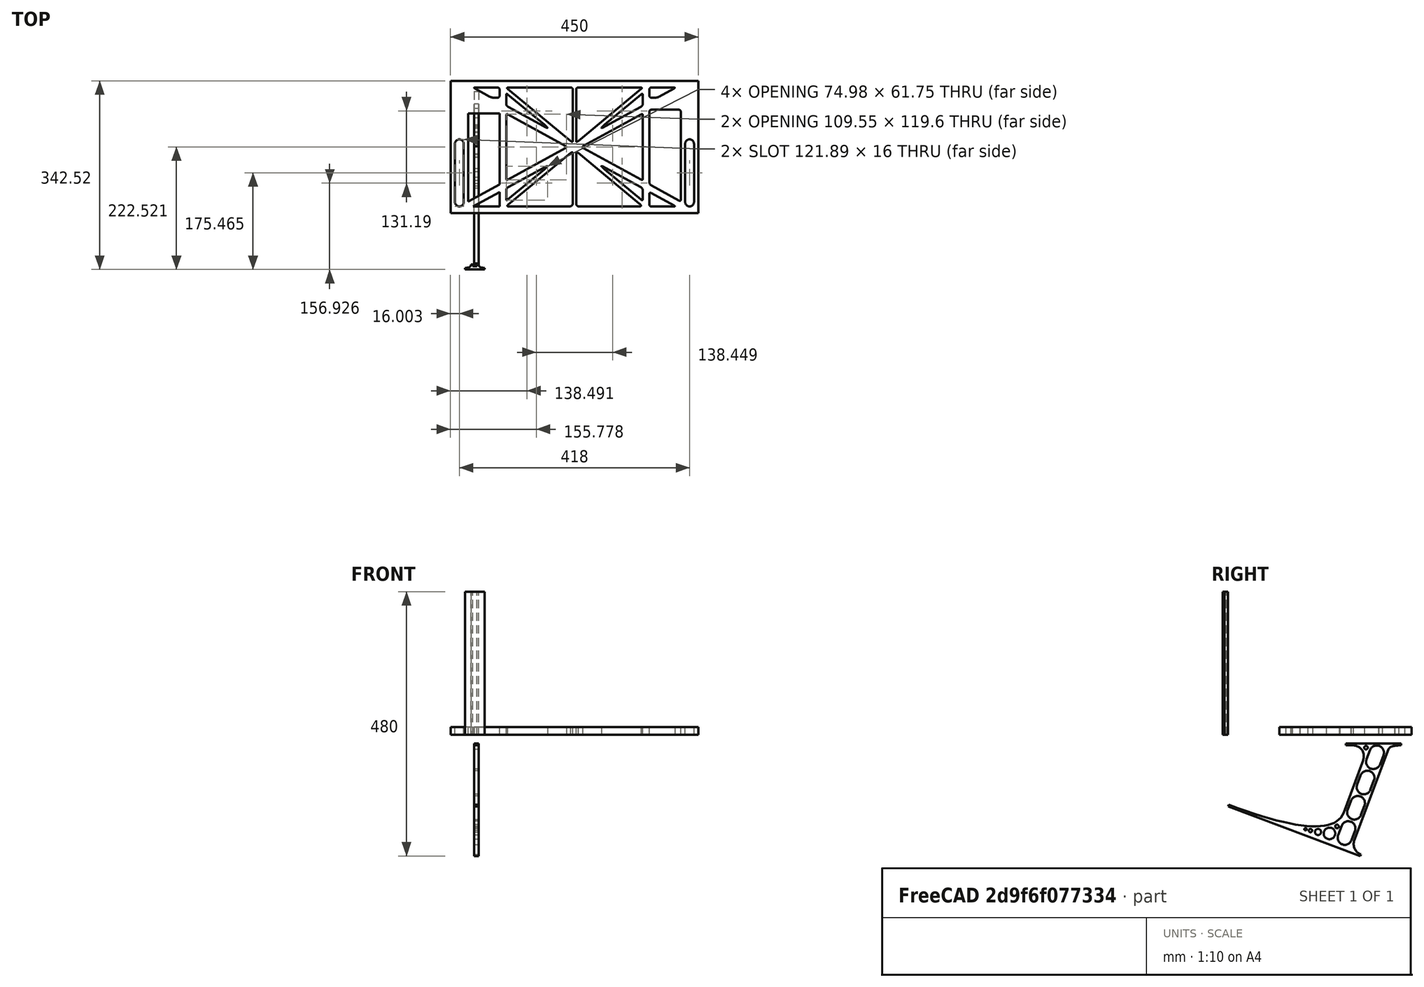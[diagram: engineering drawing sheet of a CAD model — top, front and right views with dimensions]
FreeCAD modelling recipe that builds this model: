
FCSTD DOCUMENT  (FreeCAD 0.19R0.19.2)
Label: laptopStand121FCStd
License: All rights reserved
LicenseURL: http://en.wikipedia.org/wiki/All_rights_reserved
objects: Sketcher::SketchObject×3, Part::Extrusion×3
note: 6 computed .brp shape members not serialized (recipe doc carries the construction recipe); baked Part::Feature solids carry a one-line shape summary decoded from their .brp

FEATURE [Sketcher::SketchObject] Sketch
  FullyConstrained = false
  sketch-geometry (339):
    g0: LineSegment StartX=-10.9272 StartY=-82.7794 StartZ=0 EndX=46.0728 EndY=-51.4823 EndZ=0
    g1: LineSegment StartX=-10.9272 StartY=77.3346 StartZ=0 EndX=-10.9272 EndY=-82.7794 EndZ=0
    g2: LineSegment StartX=-1.92719 StartY=-91.7794 StartZ=0 EndX=46.0728 EndY=-91.7794 EndZ=0
    g3: LineSegment StartX=46.0728 StartY=-65.424 StartZ=0 EndX=-1.92719 EndY=-91.7794 EndZ=0
    g4: LineSegment StartX=46.0728 StartY=-65.424 StartZ=0 EndX=46.0728 EndY=-91.7794 EndZ=0
    g5: LineSegment StartX=46.0728 StartY=77.3346 StartZ=0 EndX=46.0728 EndY=-51.4823 EndZ=0
    g6: LineSegment StartX=-42.9272 StartY=136.221 StartZ=0 EndX=-42.9272 EndY=-103.779 EndZ=0
    g7: LineSegment StartX=407.073 StartY=136.221 StartZ=0 EndX=407.073 EndY=-103.779 EndZ=0
    g8: ArcOfCircle CenterX=-26.9272 CenterY=22.1087 CenterZ=0 NormalX=0 NormalY=0 NormalZ=1 AngleXU=0 Radius=8 StartAngle=1e-16 EndAngle=3.14159
    g9: ArcOfCircle CenterX=-26.9272 CenterY=-83.7794 CenterZ=0 NormalX=0 NormalY=0 NormalZ=1 AngleXU=0 Radius=8 StartAngle=3.14159 EndAngle=6.28319
    g10: LineSegment StartX=-34.9272 StartY=22.1087 StartZ=0 EndX=-34.9272 EndY=-83.7794 EndZ=0
    g11: LineSegment StartX=-18.9272 StartY=22.1087 StartZ=0 EndX=-18.9272 EndY=-83.7794 EndZ=0
    g12: ArcOfCircle CenterX=391.073 CenterY=22.1087 CenterZ=0 NormalX=0 NormalY=0 NormalZ=1 AngleXU=0 Radius=8 StartAngle=-4.4e-15 EndAngle=3.14159
    g13: LineSegment StartX=399.073 StartY=22.1087 StartZ=0 EndX=399.073 EndY=-83.7794 EndZ=0
    g14: LineSegment StartX=383.073 StartY=22.1087 StartZ=0 EndX=383.073 EndY=-83.7794 EndZ=0
    g15: ArcOfCircle CenterX=391.073 CenterY=-83.7794 CenterZ=0 NormalX=0 NormalY=0 NormalZ=1 AngleXU=0 Radius=8 StartAngle=3.14159 EndAngle=6.28319
    g16: Circle CenterX=175.022 CenterY=27.0628 CenterZ=0 NormalX=0 NormalY=0 NormalZ=1 AngleXU=0 Radius=1
    g17: Circle CenterX=179.022 CenterY=24.8665 CenterZ=0 NormalX=0 NormalY=0 NormalZ=1 AngleXU=0 Radius=1
    g18: Circle CenterX=179.022 CenterY=27.0628 CenterZ=0 NormalX=0 NormalY=0 NormalZ=1 AngleXU=0 Radius=1
    g19: BSplineCurve PolesCount=3 KnotsCount=2 Degree=2 IsPeriodic=0
    g20: GeomPoint X=175.022 Y=27.0628 Z=0
    g21: GeomPoint X=179.022 Y=27.0628 Z=0
    g22: Circle CenterX=189.124 CenterY=27.0628 CenterZ=0 NormalX=0 NormalY=0 NormalZ=1 AngleXU=0 Radius=1
    g23: Circle CenterX=185.124 CenterY=24.8665 CenterZ=0 NormalX=0 NormalY=0 NormalZ=1 AngleXU=0 Radius=1
    g24: Circle CenterX=185.124 CenterY=27.0628 CenterZ=0 NormalX=0 NormalY=0 NormalZ=1 AngleXU=0 Radius=1
    g25: BSplineCurve PolesCount=3 KnotsCount=2 Degree=2 IsPeriodic=0
    g26: GeomPoint X=189.124 Y=27.0628 Z=0
    g27: GeomPoint X=185.124 Y=27.0628 Z=0
    g28: Circle CenterX=175.022 CenterY=5.37834 CenterZ=0 NormalX=0 NormalY=0 NormalZ=1 AngleXU=0 Radius=1
    g29: Circle CenterX=179.022 CenterY=7.57463 CenterZ=0 NormalX=0 NormalY=0 NormalZ=1 AngleXU=0 Radius=1
    g30: Circle CenterX=179.022 CenterY=5.34704 CenterZ=0 NormalX=0 NormalY=0 NormalZ=1 AngleXU=0 Radius=1
    g31: BSplineCurve PolesCount=3 KnotsCount=2 Degree=2 IsPeriodic=0
    g32: GeomPoint X=175.022 Y=5.37834 Z=0
    g33: GeomPoint X=179.022 Y=5.34704 Z=0
    g34: Circle CenterX=189.124 CenterY=5.37834 CenterZ=0 NormalX=0 NormalY=0 NormalZ=1 AngleXU=0 Radius=1
    g35: Circle CenterX=185.124 CenterY=7.57463 CenterZ=0 NormalX=0 NormalY=0 NormalZ=1 AngleXU=0 Radius=1
    g36: Circle CenterX=185.124 CenterY=5.34704 CenterZ=0 NormalX=0 NormalY=0 NormalZ=1 AngleXU=0 Radius=1
    g37: BSplineCurve PolesCount=3 KnotsCount=2 Degree=2 IsPeriodic=0
    g38: GeomPoint X=189.124 Y=5.37834 Z=0
    g39: GeomPoint X=185.124 Y=5.34704 Z=0
    g40: Circle CenterX=165.871 CenterY=18.1458 CenterZ=0 NormalX=0 NormalY=0 NormalZ=1 AngleXU=0 Radius=1
    g41: Circle CenterX=169.377 CenterY=16.2206 CenterZ=0 NormalX=0 NormalY=0 NormalZ=1 AngleXU=0 Radius=1
    g42: Circle CenterX=165.871 CenterY=14.2954 CenterZ=0 NormalX=0 NormalY=0 NormalZ=1 AngleXU=0 Radius=1
    g43: BSplineCurve PolesCount=3 KnotsCount=2 Degree=2 IsPeriodic=0
    g44: GeomPoint X=165.871 Y=18.1458 Z=0
    g45: GeomPoint X=165.871 Y=14.2954 Z=0
    g46: Circle CenterX=198.275 CenterY=18.1458 CenterZ=0 NormalX=0 NormalY=0 NormalZ=1 AngleXU=0 Radius=1
    g47: Circle CenterX=194.768 CenterY=16.2206 CenterZ=0 NormalX=0 NormalY=0 NormalZ=1 AngleXU=0 Radius=1
    g48: Circle CenterX=198.275 CenterY=14.2954 CenterZ=0 NormalX=0 NormalY=0 NormalZ=1 AngleXU=0 Radius=1
    g49: BSplineCurve PolesCount=3 KnotsCount=2 Degree=2 IsPeriodic=0
    g50: GeomPoint X=198.275 Y=18.1458 Z=0
    g51: GeomPoint X=198.275 Y=14.2954 Z=0
    g52: LineSegment StartX=407.073 StartY=-103.779 StartZ=0 EndX=-42.9272 EndY=-103.779 EndZ=0
    g53: LineSegment StartX=407.073 StartY=136.221 StartZ=0 EndX=-42.9272 EndY=136.221 EndZ=0
    g54: LineSegment StartX=46.0728 StartY=77.3346 StartZ=0 EndX=-10.9272 EndY=77.3346 EndZ=0
    g55: Circle CenterX=125.607 CenterY=54.1951 CenterZ=0 NormalX=0 NormalY=0 NormalZ=1 AngleXU=0 Radius=1
    g56: Circle CenterX=139.632 CenterY=46.4944 CenterZ=0 NormalX=0 NormalY=0 NormalZ=1 AngleXU=0 Radius=1
    g57: Circle CenterX=127.326 CenterY=56.7187 CenterZ=0 NormalX=0 NormalY=0 NormalZ=1 AngleXU=0 Radius=1
    g58: BSplineCurve PolesCount=3 KnotsCount=2 Degree=2 IsPeriodic=0
    g59: GeomPoint X=125.607 Y=54.1951 Z=0
    g60: GeomPoint X=127.326 Y=56.7187 Z=0
    g61: Circle CenterX=236.821 CenterY=56.7187 CenterZ=0 NormalX=0 NormalY=0 NormalZ=1 AngleXU=0 Radius=1
    g62: Circle CenterX=224.513 CenterY=46.4944 CenterZ=0 NormalX=0 NormalY=0 NormalZ=1 AngleXU=0 Radius=1
    g63: Circle CenterX=238.538 CenterY=54.1951 CenterZ=0 NormalX=0 NormalY=0 NormalZ=1 AngleXU=0 Radius=1
    g64: BSplineCurve PolesCount=3 KnotsCount=2 Degree=2 IsPeriodic=0
    g65: GeomPoint X=236.821 Y=56.7187 Z=0
    g66: GeomPoint X=238.538 Y=54.1951 Z=0
    g67: Circle CenterX=238.538 CenterY=-21.7539 CenterZ=0 NormalX=0 NormalY=0 NormalZ=1 AngleXU=0 Radius=1
    g68: Circle CenterX=224.513 CenterY=-14.0532 CenterZ=0 NormalX=0 NormalY=0 NormalZ=1 AngleXU=0 Radius=1
    g69: Circle CenterX=236.821 CenterY=-24.2775 CenterZ=0 NormalX=0 NormalY=0 NormalZ=1 AngleXU=0 Radius=1
    g70: BSplineCurve PolesCount=3 KnotsCount=2 Degree=2 IsPeriodic=0
    g71: GeomPoint X=238.538 Y=-21.7539 Z=0
    g72: GeomPoint X=236.821 Y=-24.2775 Z=0
    g73: Circle CenterX=125.607 CenterY=-21.7539 CenterZ=0 NormalX=0 NormalY=0 NormalZ=1 AngleXU=0 Radius=1
    g74: Circle CenterX=139.632 CenterY=-14.0532 CenterZ=0 NormalX=0 NormalY=0 NormalZ=1 AngleXU=0 Radius=1
    g75: Circle CenterX=127.325 CenterY=-24.2775 CenterZ=0 NormalX=0 NormalY=0 NormalZ=1 AngleXU=0 Radius=1
    g76: BSplineCurve PolesCount=3 KnotsCount=2 Degree=2 IsPeriodic=0
    g77: GeomPoint X=125.607 Y=-21.7539 Z=0
    g78: GeomPoint X=127.325 Y=-24.2775 Z=0
    g79: Circle CenterX=302.996 CenterY=111.695 CenterZ=0 NormalX=0 NormalY=0 NormalZ=1 AngleXU=0 Radius=1
    g80: Circle CenterX=306.073 CenterY=114.251 CenterZ=0 NormalX=0 NormalY=0 NormalZ=1 AngleXU=0 Radius=1
    g81: Circle CenterX=306.073 CenterY=110.251 CenterZ=0 NormalX=0 NormalY=0 NormalZ=1 AngleXU=0 Radius=1
    g82: BSplineCurve PolesCount=3 KnotsCount=2 Degree=2 IsPeriodic=0
    g83: GeomPoint X=302.996 Y=111.695 Z=0
    g84: GeomPoint X=306.073 Y=110.251 Z=0
    g85: Circle CenterX=306.073 CenterY=95.2763 CenterZ=0 NormalX=0 NormalY=0 NormalZ=1 AngleXU=0 Radius=1
    g86: Circle CenterX=306.073 CenterY=91.2763 CenterZ=0 NormalX=0 NormalY=0 NormalZ=1 AngleXU=0 Radius=1
    g87: Circle CenterX=302.567 CenterY=89.3511 CenterZ=0 NormalX=0 NormalY=0 NormalZ=1 AngleXU=0 Radius=1
    g88: BSplineCurve PolesCount=3 KnotsCount=2 Degree=2 IsPeriodic=0
    g89: GeomPoint X=306.073 Y=95.2763 Z=0
    g90: GeomPoint X=302.567 Y=89.3511 Z=0
    g91: LineSegment StartX=306.073 StartY=110.251 StartZ=0 EndX=306.073 EndY=95.2763 EndZ=0
    g92: LineSegment StartX=302.996 StartY=111.695 StartZ=0 EndX=236.821 EndY=56.7187 EndZ=0
    g93: LineSegment StartX=238.538 StartY=54.1951 StartZ=0 EndX=302.567 EndY=89.3511 EndZ=0
    g94: Circle CenterX=61.1496 CenterY=111.695 CenterZ=0 NormalX=0 NormalY=0 NormalZ=1 AngleXU=0 Radius=1
    g95: Circle CenterX=58.0728 CenterY=114.251 CenterZ=0 NormalX=0 NormalY=0 NormalZ=1 AngleXU=0 Radius=1
    g96: Circle CenterX=58.0728 CenterY=110.251 CenterZ=0 NormalX=0 NormalY=0 NormalZ=1 AngleXU=0 Radius=1
    g97: BSplineCurve PolesCount=3 KnotsCount=2 Degree=2 IsPeriodic=0
    g98: GeomPoint X=61.1496 Y=111.695 Z=0
    g99: GeomPoint X=58.0728 Y=110.251 Z=0
    g100: Circle CenterX=61.5791 CenterY=89.3511 CenterZ=0 NormalX=0 NormalY=0 NormalZ=1 AngleXU=0 Radius=1
    g101: Circle CenterX=58.0728 CenterY=91.2763 CenterZ=0 NormalX=0 NormalY=0 NormalZ=1 AngleXU=0 Radius=1
    g102: Circle CenterX=58.0728 CenterY=95.2763 CenterZ=0 NormalX=0 NormalY=0 NormalZ=1 AngleXU=0 Radius=1
    g103: BSplineCurve PolesCount=3 KnotsCount=2 Degree=2 IsPeriodic=0
    g104: GeomPoint X=61.5791 Y=89.3511 Z=0
    g105: GeomPoint X=58.0728 Y=95.2763 Z=0
    g106: LineSegment StartX=58.0728 StartY=110.251 StartZ=0 EndX=58.0728 EndY=95.2763 EndZ=0
    g107: LineSegment StartX=61.1496 StartY=111.695 StartZ=0 EndX=127.326 EndY=56.7187 EndZ=0
    g108: LineSegment StartX=125.607 StartY=54.1951 StartZ=0 EndX=61.5791 EndY=89.3511 EndZ=0
    g109: Circle CenterX=61.5791 CenterY=-56.9099 CenterZ=0 NormalX=0 NormalY=0 NormalZ=1 AngleXU=0 Radius=1
    g110: Circle CenterX=58.0728 CenterY=-58.8351 CenterZ=0 NormalX=0 NormalY=0 NormalZ=1 AngleXU=0 Radius=1
    g111: Circle CenterX=58.0728 CenterY=-62.8351 CenterZ=0 NormalX=0 NormalY=0 NormalZ=1 AngleXU=0 Radius=1
    g112: BSplineCurve PolesCount=3 KnotsCount=2 Degree=2 IsPeriodic=0
    g113: GeomPoint X=61.5791 Y=-56.9099 Z=0
    g114: GeomPoint X=58.0728 Y=-62.8351 Z=0
    g115: Circle CenterX=58.0728 CenterY=-77.8102 CenterZ=0 NormalX=0 NormalY=0 NormalZ=1 AngleXU=0 Radius=1
    g116: Circle CenterX=58.0728 CenterY=-81.8102 CenterZ=0 NormalX=0 NormalY=0 NormalZ=1 AngleXU=0 Radius=1
    g117: Circle CenterX=61.1496 CenterY=-79.2541 CenterZ=0 NormalX=0 NormalY=0 NormalZ=1 AngleXU=0 Radius=1
    g118: BSplineCurve PolesCount=3 KnotsCount=2 Degree=2 IsPeriodic=0
    g119: GeomPoint X=58.0728 Y=-77.8102 Z=0
    g120: GeomPoint X=61.1496 Y=-79.2541 Z=0
    g121: LineSegment StartX=58.0728 StartY=-62.8351 StartZ=0 EndX=58.0728 EndY=-77.8102 EndZ=0
    g122: LineSegment StartX=61.1496 StartY=-79.2541 StartZ=0 EndX=127.325 EndY=-24.2775 EndZ=0
    g123: LineSegment StartX=125.607 StartY=-21.7539 StartZ=0 EndX=61.5791 EndY=-56.9099 EndZ=0
    g124: Circle CenterX=302.567 CenterY=-56.9099 CenterZ=0 NormalX=0 NormalY=0 NormalZ=1 AngleXU=0 Radius=1
    g125: Circle CenterX=306.073 CenterY=-58.8351 CenterZ=0 NormalX=0 NormalY=0 NormalZ=1 AngleXU=0 Radius=1
    g126: Circle CenterX=306.073 CenterY=-62.8351 CenterZ=0 NormalX=0 NormalY=0 NormalZ=1 AngleXU=0 Radius=1
    g127: BSplineCurve PolesCount=3 KnotsCount=2 Degree=2 IsPeriodic=0
    g128: GeomPoint X=302.567 Y=-56.9099 Z=0
    g129: GeomPoint X=306.073 Y=-62.8351 Z=0
    g130: Circle CenterX=302.996 CenterY=-79.2541 CenterZ=0 NormalX=0 NormalY=0 NormalZ=1 AngleXU=0 Radius=1
    g131: Circle CenterX=306.073 CenterY=-81.8102 CenterZ=0 NormalX=0 NormalY=0 NormalZ=1 AngleXU=0 Radius=1
    g132: Circle CenterX=306.073 CenterY=-77.8102 CenterZ=0 NormalX=0 NormalY=0 NormalZ=1 AngleXU=0 Radius=1
    g133: BSplineCurve PolesCount=3 KnotsCount=2 Degree=2 IsPeriodic=0
    g134: GeomPoint X=302.996 Y=-79.2541 Z=0
    g135: GeomPoint X=306.073 Y=-77.8102 Z=0
    g136: LineSegment StartX=306.073 StartY=-62.8351 StartZ=0 EndX=306.073 EndY=-77.8102 EndZ=0
    g137: LineSegment StartX=302.996 StartY=-79.2541 StartZ=0 EndX=236.821 EndY=-24.2775 EndZ=0
    g138: LineSegment StartX=238.538 StartY=-21.7539 StartZ=0 EndX=302.567 EndY=-56.9099 EndZ=0
    g139: Circle CenterX=61.6457 CenterY=-88.8112 CenterZ=0 NormalX=0 NormalY=0 NormalZ=1 AngleXU=0 Radius=1
    g140: Circle CenterX=58.0728 CenterY=-91.7794 CenterZ=0 NormalX=0 NormalY=0 NormalZ=1 AngleXU=0 Radius=1
    g141: Circle CenterX=63.9135 CenterY=-91.7794 CenterZ=0 NormalX=0 NormalY=0 NormalZ=1 AngleXU=0 Radius=1
    g142: BSplineCurve PolesCount=3 KnotsCount=2 Degree=2 IsPeriodic=0
    g143: GeomPoint X=61.6457 Y=-88.8112 Z=0
    g144: GeomPoint X=63.9135 Y=-91.7794 Z=0
    g145: Circle CenterX=179.022 CenterY=-85.8163 CenterZ=0 NormalX=0 NormalY=0 NormalZ=1 AngleXU=0 Radius=1
    g146: Circle CenterX=179.022 CenterY=-91.7794 CenterZ=0 NormalX=0 NormalY=0 NormalZ=1 AngleXU=0 Radius=1
    g147: Circle CenterX=171.895 CenterY=-91.7794 CenterZ=0 NormalX=0 NormalY=0 NormalZ=1 AngleXU=0 Radius=1
    g148: BSplineCurve PolesCount=3 KnotsCount=2 Degree=2 IsPeriodic=0
    g149: GeomPoint X=179.022 Y=-85.8163 Z=0
    g150: GeomPoint X=171.895 Y=-91.7794 Z=0
    g151: Circle CenterX=185.124 CenterY=-86.2028 CenterZ=0 NormalX=0 NormalY=0 NormalZ=1 AngleXU=0 Radius=1
    g152: Circle CenterX=185.124 CenterY=-91.7794 CenterZ=0 NormalX=0 NormalY=0 NormalZ=1 AngleXU=0 Radius=1
    g153: Circle CenterX=191.747 CenterY=-91.7794 CenterZ=0 NormalX=0 NormalY=0 NormalZ=1 AngleXU=0 Radius=1
    g154: BSplineCurve PolesCount=3 KnotsCount=2 Degree=2 IsPeriodic=0
    g155: GeomPoint X=185.124 Y=-86.2028 Z=0
    g156: GeomPoint X=191.747 Y=-91.7794 Z=0
    g157: Circle CenterX=299.888 CenterY=-86.6413 CenterZ=0 NormalX=0 NormalY=0 NormalZ=1 AngleXU=0 Radius=1
    g158: Circle CenterX=306.073 CenterY=-91.7794 CenterZ=0 NormalX=0 NormalY=0 NormalZ=1 AngleXU=0 Radius=1
    g159: Circle CenterX=298.776 CenterY=-91.7794 CenterZ=0 NormalX=0 NormalY=0 NormalZ=1 AngleXU=0 Radius=1
    g160: BSplineCurve PolesCount=3 KnotsCount=2 Degree=2 IsPeriodic=0
    g161: GeomPoint X=299.888 Y=-86.6413 Z=0
    g162: GeomPoint X=298.776 Y=-91.7794 Z=0
    g163: LineSegment StartX=189.124 StartY=5.37834 StartZ=0 EndX=299.888 EndY=-86.6413 EndZ=0
    g164: LineSegment StartX=298.776 StartY=-91.7794 StartZ=0 EndX=191.747 EndY=-91.7794 EndZ=0
    g165: LineSegment StartX=185.124 StartY=-86.2028 StartZ=0 EndX=185.124 EndY=5.34704 EndZ=0
    g166: LineSegment StartX=179.022 StartY=5.34704 StartZ=0 EndX=179.022 EndY=-85.8163 EndZ=0
    g167: LineSegment StartX=171.895 StartY=-91.7794 StartZ=0 EndX=63.9135 EndY=-91.7794 EndZ=0
    g168: LineSegment StartX=61.6457 StartY=-88.8112 StartZ=0 EndX=175.022 EndY=5.37834 EndZ=0
    g169: Circle CenterX=302.073 CenterY=124.221 CenterZ=0 NormalX=0 NormalY=0 NormalZ=1 AngleXU=0 Radius=1
    g170: Circle CenterX=306.073 CenterY=124.221 CenterZ=0 NormalX=0 NormalY=0 NormalZ=1 AngleXU=0 Radius=1
    g171: Circle CenterX=302.996 CenterY=121.665 CenterZ=0 NormalX=0 NormalY=0 NormalZ=1 AngleXU=0 Radius=1
    g172: BSplineCurve PolesCount=3 KnotsCount=2 Degree=2 IsPeriodic=0
    g173: GeomPoint X=302.073 Y=124.221 Z=0
    g174: GeomPoint X=302.996 Y=121.665 Z=0
    g175: Circle CenterX=189.124 CenterY=124.221 CenterZ=0 NormalX=0 NormalY=0 NormalZ=1 AngleXU=0 Radius=1
    g176: Circle CenterX=185.124 CenterY=124.221 CenterZ=0 NormalX=0 NormalY=0 NormalZ=1 AngleXU=0 Radius=1
    g177: Circle CenterX=185.124 CenterY=120.221 CenterZ=0 NormalX=0 NormalY=0 NormalZ=1 AngleXU=0 Radius=1
    g178: BSplineCurve PolesCount=3 KnotsCount=2 Degree=2 IsPeriodic=0
    g179: GeomPoint X=189.124 Y=124.221 Z=0
    g180: GeomPoint X=185.124 Y=120.221 Z=0
    g181: Circle CenterX=175.022 CenterY=124.221 CenterZ=0 NormalX=0 NormalY=0 NormalZ=1 AngleXU=0 Radius=1
    g182: Circle CenterX=179.022 CenterY=124.221 CenterZ=0 NormalX=0 NormalY=0 NormalZ=1 AngleXU=0 Radius=1
    g183: Circle CenterX=179.022 CenterY=120.221 CenterZ=0 NormalX=0 NormalY=0 NormalZ=1 AngleXU=0 Radius=1
    g184: BSplineCurve PolesCount=3 KnotsCount=2 Degree=2 IsPeriodic=0
    g185: GeomPoint X=175.022 Y=124.221 Z=0
    g186: GeomPoint X=179.022 Y=120.221 Z=0
    g187: Circle CenterX=62.0728 CenterY=124.221 CenterZ=0 NormalX=0 NormalY=0 NormalZ=1 AngleXU=0 Radius=1
    g188: Circle CenterX=58.0728 CenterY=124.221 CenterZ=0 NormalX=0 NormalY=0 NormalZ=1 AngleXU=0 Radius=1
    g189: Circle CenterX=61.1496 CenterY=121.665 CenterZ=0 NormalX=0 NormalY=0 NormalZ=1 AngleXU=0 Radius=1
    g190: BSplineCurve PolesCount=3 KnotsCount=2 Degree=2 IsPeriodic=0
    g191: GeomPoint X=62.0728 Y=124.221 Z=0
    g192: GeomPoint X=61.1496 Y=121.665 Z=0
    g193: LineSegment StartX=62.0728 StartY=124.221 StartZ=0 EndX=175.022 EndY=124.221 EndZ=0
    g194: LineSegment StartX=179.022 StartY=120.221 StartZ=0 EndX=179.022 EndY=27.0628 EndZ=0
    g195: LineSegment StartX=185.124 StartY=27.0628 StartZ=0 EndX=185.124 EndY=120.221 EndZ=0
    g196: LineSegment StartX=189.124 StartY=124.221 StartZ=0 EndX=302.073 EndY=124.221 EndZ=0
    g197: LineSegment StartX=302.996 StartY=121.665 StartZ=0 EndX=189.124 EndY=27.0628 EndZ=0
    g198: LineSegment StartX=175.022 StartY=27.0628 StartZ=0 EndX=61.1496 EndY=121.665 EndZ=0
    g199: Circle CenterX=61.5791 CenterY=75.4095 CenterZ=0 NormalX=0 NormalY=0 NormalZ=1 AngleXU=0 Radius=1
    g200: Circle CenterX=58.0728 CenterY=77.3346 CenterZ=0 NormalX=0 NormalY=0 NormalZ=1 AngleXU=0 Radius=1
    g201: Circle CenterX=58.0728 CenterY=73.3346 CenterZ=0 NormalX=0 NormalY=0 NormalZ=1 AngleXU=0 Radius=1
    g202: BSplineCurve PolesCount=3 KnotsCount=2 Degree=2 IsPeriodic=0
    g203: GeomPoint X=61.5791 Y=75.4095 Z=0
    g204: GeomPoint X=58.0728 Y=73.3346 Z=0
    g205: Circle CenterX=58.0728 CenterY=-40.8935 CenterZ=0 NormalX=0 NormalY=0 NormalZ=1 AngleXU=0 Radius=1
    g206: Circle CenterX=58.0728 CenterY=-44.8935 CenterZ=0 NormalX=0 NormalY=0 NormalZ=1 AngleXU=0 Radius=1
    g207: Circle CenterX=61.5791 CenterY=-42.9683 CenterZ=0 NormalX=0 NormalY=0 NormalZ=1 AngleXU=0 Radius=1
    g208: BSplineCurve PolesCount=3 KnotsCount=2 Degree=2 IsPeriodic=0
    g209: GeomPoint X=58.0728 Y=-40.8935 Z=0
    g210: GeomPoint X=61.5791 Y=-42.9683 Z=0
    g211: LineSegment StartX=61.5791 StartY=-42.9683 StartZ=0 EndX=165.871 EndY=14.2954 EndZ=0
    g212: LineSegment StartX=165.871 StartY=18.1458 StartZ=0 EndX=61.5791 EndY=75.4095 EndZ=0
    g213: LineSegment StartX=58.0728 StartY=73.3346 StartZ=0 EndX=58.0728 EndY=-40.8935 EndZ=0
    g214: Circle CenterX=302.567 CenterY=-42.9683 CenterZ=0 NormalX=0 NormalY=0 NormalZ=1 AngleXU=0 Radius=1
    g215: Circle CenterX=306.073 CenterY=-44.8935 CenterZ=0 NormalX=0 NormalY=0 NormalZ=1 AngleXU=0 Radius=1
    g216: Circle CenterX=306.073 CenterY=-40.8935 CenterZ=0 NormalX=0 NormalY=0 NormalZ=1 AngleXU=0 Radius=1
    g217: BSplineCurve PolesCount=3 KnotsCount=2 Degree=2 IsPeriodic=0
    g218: GeomPoint X=302.567 Y=-42.9683 Z=0
    g219: GeomPoint X=306.073 Y=-40.8935 Z=0
    g220: Circle CenterX=306.073 CenterY=73.3346 CenterZ=0 NormalX=0 NormalY=0 NormalZ=1 AngleXU=0 Radius=1
    g221: Circle CenterX=306.073 CenterY=77.3346 CenterZ=0 NormalX=0 NormalY=0 NormalZ=1 AngleXU=0 Radius=1
    g222: Circle CenterX=302.567 CenterY=75.4095 CenterZ=0 NormalX=0 NormalY=0 NormalZ=1 AngleXU=0 Radius=1
    g223: BSplineCurve PolesCount=3 KnotsCount=2 Degree=2 IsPeriodic=0
    g224: GeomPoint X=306.073 Y=73.3346 Z=0
    g225: GeomPoint X=302.567 Y=75.4095 Z=0
    g226: LineSegment StartX=302.567 StartY=-42.9683 StartZ=0 EndX=198.275 EndY=14.2954 EndZ=0
    g227: LineSegment StartX=198.275 StartY=18.1458 StartZ=0 EndX=302.567 EndY=75.4095 EndZ=0
    g228: LineSegment StartX=306.073 StartY=73.3346 StartZ=0 EndX=306.073 EndY=-40.8935 EndZ=0
    g229: LineSegment StartX=322.073 StartY=105.865 StartZ=0 EndX=328.643 EndY=105.865 EndZ=0
    g230: LineSegment StartX=318.073 StartY=120.221 StartZ=0 EndX=318.073 EndY=109.865 EndZ=0
    g231: LineSegment StartX=336.157 StartY=107.779 StartZ=0 EndX=362.567 EndY=122.294 EndZ=0
    g232: Circle CenterX=362.073 CenterY=124.221 CenterZ=0 NormalX=0 NormalY=0 NormalZ=1 AngleXU=0 Radius=1
    g233: Circle CenterX=366.073 CenterY=124.221 CenterZ=0 NormalX=0 NormalY=0 NormalZ=1 AngleXU=0 Radius=1
    g234: Circle CenterX=362.567 CenterY=122.294 CenterZ=0 NormalX=0 NormalY=0 NormalZ=1 AngleXU=0 Radius=1
    g235: BSplineCurve PolesCount=3 KnotsCount=2 Degree=2 IsPeriodic=0
    g236: GeomPoint X=362.073 Y=124.221 Z=0
    g237: GeomPoint X=362.567 Y=122.294 Z=0
    g238: Circle CenterX=322.073 CenterY=124.221 CenterZ=0 NormalX=0 NormalY=0 NormalZ=1 AngleXU=0 Radius=1
    g239: Circle CenterX=318.073 CenterY=124.221 CenterZ=0 NormalX=0 NormalY=0 NormalZ=1 AngleXU=0 Radius=1
    g240: Circle CenterX=318.073 CenterY=120.221 CenterZ=0 NormalX=0 NormalY=0 NormalZ=1 AngleXU=0 Radius=1
    g241: BSplineCurve PolesCount=3 KnotsCount=2 Degree=2 IsPeriodic=0
    g242: GeomPoint X=322.073 Y=124.221 Z=0
    g243: GeomPoint X=318.073 Y=120.221 Z=0
    g244: Circle CenterX=322.073 CenterY=105.865 CenterZ=0 NormalX=0 NormalY=0 NormalZ=1 AngleXU=0 Radius=1
    g245: Circle CenterX=318.073 CenterY=105.865 CenterZ=0 NormalX=0 NormalY=0 NormalZ=1 AngleXU=0 Radius=1
    g246: Circle CenterX=318.073 CenterY=109.865 CenterZ=0 NormalX=0 NormalY=0 NormalZ=1 AngleXU=0 Radius=1
    g247: BSplineCurve PolesCount=3 KnotsCount=2 Degree=2 IsPeriodic=0
    g248: GeomPoint X=322.073 Y=105.865 Z=0
    g249: GeomPoint X=318.073 Y=109.865 Z=0
    g250: Circle CenterX=336.157 CenterY=107.779 CenterZ=0 NormalX=0 NormalY=0 NormalZ=1 AngleXU=0 Radius=1
    g251: Circle CenterX=332.651 CenterY=105.853 CenterZ=0 NormalX=0 NormalY=0 NormalZ=1 AngleXU=0 Radius=1
    g252: Circle CenterX=328.643 CenterY=105.865 CenterZ=0 NormalX=0 NormalY=0 NormalZ=1 AngleXU=0 Radius=1
    g253: BSplineCurve PolesCount=3 KnotsCount=2 Degree=2 IsPeriodic=0
    g254: GeomPoint X=336.157 Y=107.779 Z=0
    g255: GeomPoint X=328.643 Y=105.865 Z=0
    g256: LineSegment StartX=322.073 StartY=124.221 StartZ=0 EndX=362.073 EndY=124.221 EndZ=0
    g257: Circle CenterX=371.567 CenterY=-80.8644 CenterZ=0 NormalX=0 NormalY=0 NormalZ=1 AngleXU=0 Radius=1
    g258: Circle CenterX=375.073 CenterY=-82.7896 CenterZ=0 NormalX=0 NormalY=0 NormalZ=1 AngleXU=0 Radius=1
    g259: Circle CenterX=375.073 CenterY=-78.7896 CenterZ=0 NormalX=0 NormalY=0 NormalZ=1 AngleXU=0 Radius=1
    g260: BSplineCurve PolesCount=3 KnotsCount=2 Degree=2 IsPeriodic=0
    g261: GeomPoint X=371.567 Y=-80.8644 Z=0
    g262: GeomPoint X=375.073 Y=-78.7896 Z=0
    g263: Circle CenterX=321.579 CenterY=-53.4075 CenterZ=0 NormalX=0 NormalY=0 NormalZ=1 AngleXU=0 Radius=1
    g264: Circle CenterX=318.073 CenterY=-51.4823 CenterZ=0 NormalX=0 NormalY=0 NormalZ=1 AngleXU=0 Radius=1
    g265: Circle CenterX=318.073 CenterY=-47.4823 CenterZ=0 NormalX=0 NormalY=0 NormalZ=1 AngleXU=0 Radius=1
    g266: BSplineCurve PolesCount=3 KnotsCount=2 Degree=2 IsPeriodic=0
    g267: GeomPoint X=321.579 Y=-53.4075 Z=0
    g268: GeomPoint X=318.073 Y=-47.4823 Z=0
    g269: Circle CenterX=318.073 CenterY=79.9235 CenterZ=0 NormalX=0 NormalY=0 NormalZ=1 AngleXU=0 Radius=1
    g270: Circle CenterX=318.073 CenterY=83.9235 CenterZ=0 NormalX=0 NormalY=0 NormalZ=1 AngleXU=0 Radius=1
    g271: Circle CenterX=322.073 CenterY=83.9235 CenterZ=0 NormalX=0 NormalY=0 NormalZ=1 AngleXU=0 Radius=1
    g272: BSplineCurve PolesCount=3 KnotsCount=2 Degree=2 IsPeriodic=0
    g273: GeomPoint X=318.073 Y=79.9235 Z=0
    g274: GeomPoint X=322.073 Y=83.9235 Z=0
    g275: Circle CenterX=375.073 CenterY=79.9235 CenterZ=0 NormalX=0 NormalY=0 NormalZ=1 AngleXU=0 Radius=1
    g276: Circle CenterX=375.073 CenterY=83.9235 CenterZ=0 NormalX=0 NormalY=0 NormalZ=1 AngleXU=0 Radius=1
    g277: Circle CenterX=371.073 CenterY=83.9235 CenterZ=0 NormalX=0 NormalY=0 NormalZ=1 AngleXU=0 Radius=1
    g278: BSplineCurve PolesCount=3 KnotsCount=2 Degree=2 IsPeriodic=0
    g279: GeomPoint X=375.073 Y=79.9235 Z=0
    g280: GeomPoint X=371.073 Y=83.9235 Z=0
    g281: LineSegment StartX=322.073 StartY=83.9235 StartZ=0 EndX=371.073 EndY=83.9235 EndZ=0
    g282: LineSegment StartX=375.073 StartY=79.9235 StartZ=0 EndX=375.073 EndY=-78.7896 EndZ=0
    g283: LineSegment StartX=371.567 StartY=-80.8644 StartZ=0 EndX=321.579 EndY=-53.4075 EndZ=0
    g284: LineSegment StartX=318.073 StartY=-47.4823 StartZ=0 EndX=318.073 EndY=79.9235 EndZ=0
    g285: Circle CenterX=321.579 CenterY=-67.3492 CenterZ=0 NormalX=0 NormalY=0 NormalZ=1 AngleXU=0 Radius=1
    g286: Circle CenterX=318.073 CenterY=-65.424 CenterZ=0 NormalX=0 NormalY=0 NormalZ=1 AngleXU=0 Radius=1
    g287: Circle CenterX=318.073 CenterY=-69.424 CenterZ=0 NormalX=0 NormalY=0 NormalZ=1 AngleXU=0 Radius=1
    g288: BSplineCurve PolesCount=3 KnotsCount=2 Degree=2 IsPeriodic=0
    g289: GeomPoint X=321.579 Y=-67.3492 Z=0
    g290: GeomPoint X=318.073 Y=-69.424 Z=0
    g291: Circle CenterX=362.567 CenterY=-89.8542 CenterZ=0 NormalX=0 NormalY=0 NormalZ=1 AngleXU=0 Radius=1
    g292: Circle CenterX=366.073 CenterY=-91.7794 CenterZ=0 NormalX=0 NormalY=0 NormalZ=1 AngleXU=0 Radius=1
    g293: Circle CenterX=362.073 CenterY=-91.7794 CenterZ=0 NormalX=0 NormalY=0 NormalZ=1 AngleXU=0 Radius=1
    g294: BSplineCurve PolesCount=3 KnotsCount=2 Degree=2 IsPeriodic=0
    g295: GeomPoint X=362.567 Y=-89.8542 Z=0
    g296: GeomPoint X=362.073 Y=-91.7794 Z=0
    g297: Circle CenterX=322.073 CenterY=-91.7794 CenterZ=0 NormalX=0 NormalY=0 NormalZ=1 AngleXU=0 Radius=1
    g298: Circle CenterX=318.073 CenterY=-91.7794 CenterZ=0 NormalX=0 NormalY=0 NormalZ=1 AngleXU=0 Radius=1
    g299: Circle CenterX=318.073 CenterY=-87.7794 CenterZ=0 NormalX=0 NormalY=0 NormalZ=1 AngleXU=0 Radius=1
    g300: BSplineCurve PolesCount=3 KnotsCount=2 Degree=2 IsPeriodic=0
    g301: GeomPoint X=322.073 Y=-91.7794 Z=0
    g302: GeomPoint X=318.073 Y=-87.7794 Z=0
    g303: LineSegment StartX=362.567 StartY=-89.8542 StartZ=0 EndX=321.579 EndY=-67.3492 EndZ=0
    g304: LineSegment StartX=318.073 StartY=-69.424 StartZ=0 EndX=318.073 EndY=-87.7794 EndZ=0
    g305: LineSegment StartX=322.073 StartY=-91.7794 StartZ=0 EndX=362.073 EndY=-91.7794 EndZ=0
    g306: Circle CenterX=2.07281 CenterY=124.221 CenterZ=0 NormalX=0 NormalY=0 NormalZ=1 AngleXU=0 Radius=1
    g307: Circle CenterX=1.57905 CenterY=122.295 CenterZ=0 NormalX=0 NormalY=0 NormalZ=1 AngleXU=0 Radius=1
    g308: BSplineCurve PolesCount=3 KnotsCount=2 Degree=2 IsPeriodic=0
    g309: GeomPoint X=2.07281 Y=124.221 Z=0
    g310: GeomPoint X=1.57905 Y=122.295 Z=0
    g311: Circle CenterX=42.0728 CenterY=124.221 CenterZ=0 NormalX=0 NormalY=0 NormalZ=1 AngleXU=0 Radius=1
    g312: Circle CenterX=46.0728 CenterY=124.221 CenterZ=0 NormalX=0 NormalY=0 NormalZ=1 AngleXU=0 Radius=1
    g313: Circle CenterX=46.0728 CenterY=120.221 CenterZ=0 NormalX=0 NormalY=0 NormalZ=1 AngleXU=0 Radius=1
    g314: BSplineCurve PolesCount=3 KnotsCount=2 Degree=2 IsPeriodic=0
    g315: GeomPoint X=42.0728 Y=124.221 Z=0
    g316: GeomPoint X=46.0728 Y=120.221 Z=0
    g317: Circle CenterX=46.0728 CenterY=109.865 CenterZ=0 NormalX=0 NormalY=0 NormalZ=1 AngleXU=0 Radius=1
    g318: Circle CenterX=46.0728 CenterY=105.865 CenterZ=0 NormalX=0 NormalY=0 NormalZ=1 AngleXU=0 Radius=1
    g319: Circle CenterX=42.0728 CenterY=105.865 CenterZ=0 NormalX=0 NormalY=0 NormalZ=1 AngleXU=0 Radius=1
    g320: BSplineCurve PolesCount=3 KnotsCount=2 Degree=2 IsPeriodic=0
    g321: GeomPoint X=46.0728 Y=109.865 Z=0
    g322: GeomPoint X=42.0728 Y=105.865 Z=0
    g323: Circle CenterX=35.5028 CenterY=105.865 CenterZ=0 NormalX=0 NormalY=0 NormalZ=1 AngleXU=0 Radius=1
    g324: Circle CenterX=31.5028 CenterY=105.865 CenterZ=0 NormalX=0 NormalY=0 NormalZ=1 AngleXU=0 Radius=1
    g325: Circle CenterX=27.9965 CenterY=107.79 CenterZ=0 NormalX=0 NormalY=0 NormalZ=1 AngleXU=0 Radius=1
    g326: BSplineCurve PolesCount=3 KnotsCount=2 Degree=2 IsPeriodic=0
    g327: GeomPoint X=35.5028 Y=105.865 Z=0
    g328: GeomPoint X=27.9965 Y=107.79 Z=0
    g329: LineSegment StartX=2.07281 StartY=124.221 StartZ=0 EndX=42.0728 EndY=124.221 EndZ=0
    g330: LineSegment StartX=46.0728 StartY=120.221 StartZ=0 EndX=46.0728 EndY=109.865 EndZ=0
    g331: LineSegment StartX=42.0728 StartY=105.865 StartZ=0 EndX=35.5028 EndY=105.865 EndZ=0
    g332: LineSegment StartX=27.9965 StartY=107.79 StartZ=0 EndX=1.57905 EndY=122.295 EndZ=0
    g333: LineSegment StartX=47.176 StartY=-65.9694 StartZ=0 EndX=47.176 EndY=-69.9694 EndZ=0
    g334: LineSegment StartX=47.422 StartY=-90.8018 StartZ=0 EndX=47.422 EndY=-86.8018 EndZ=0
    g335: LineSegment StartX=44.4314 StartY=-93.195 StartZ=0 EndX=40.4314 EndY=-93.195 EndZ=0
    g336: LineSegment StartX=-0.556681 StartY=-92.6679 StartZ=0 EndX=3.44332 EndY=-92.6679 EndZ=0
    g337: LineSegment StartX=-0.985737 StartY=-90.2701 StartZ=0 EndX=2.5205 EndY=-88.345 EndZ=0
    g338: LineSegment StartX=45.3223 StartY=-64.9652 StartZ=0 EndX=41.8161 EndY=-66.8904 EndZ=0
  constraints (564):
    c: Horizontal(g2)
    c: Coincident(g4,g3)
    c: Coincident(g0,g5)
    c: Block(g4)
    c: Block(g3)
    c: Block(g0)
    c: Block(g1)
    c: Block(g2)
    c: Vertical(g6)
    c: Vertical(g7)
    c: Block(g7)
    c: Block(g6)
    c: Tangent(g8,g11) = 1.5708
    c: Tangent(g8,g10) = -1.5708
    c: Tangent(g10,g9) = -1.5708
    c: Tangent(g11,g9) = 1.5708
    c: Vertical(g10)
    c: Equal(g8,g9)
    c: Block(g11)
    c: Block(g10)
    c: Tangent(g12,g13) = 1.5708
    c: Tangent(g13,g15) = 1.5708
    c: Equal(g12,g15)
    c: Coincident(g14,g12)
    c: Coincident(g14,g15)
    c: Block(g13)
    c: Block(g14)
    c: Weight(g16) = 1
    c: Equal(g16,g17)
    c: Equal(g16,g18)
    c: InternalAlignment(g16,g19)
    c: InternalAlignment(g17,g19)
    c: InternalAlignment(g18,g19)
    c: InternalAlignment(g20,g19)
    c: InternalAlignment(g21,g19)
    c: Weight(g22) = 1
    c: Equal(g22,g23)
    c: Equal(g22,g24)
    c: InternalAlignment(g22,g25)
    c: InternalAlignment(g23,g25)
    c: InternalAlignment(g24,g25)
    c: InternalAlignment(g26,g25)
    c: InternalAlignment(g27,g25)
    c: Block(g25)
    c: Block(g19)
    c: Weight(g28) = 1
    c: Equal(g28,g29)
    c: Equal(g28,g30)
    c: InternalAlignment(g28,g31)
    c: InternalAlignment(g29,g31)
    c: InternalAlignment(g30,g31)
    c: InternalAlignment(g32,g31)
    c: InternalAlignment(g33,g31)
    c: Weight(g34) = 1
    c: Equal(g34,g35)
    c: Equal(g34,g36)
    c: InternalAlignment(g34,g37)
    c: InternalAlignment(g35,g37)
    c: InternalAlignment(g36,g37)
    c: InternalAlignment(g38,g37)
    c: InternalAlignment(g39,g37)
    c: Block(g37)
    c: Block(g31)
    c: Weight(g40) = 1
    c: Equal(g40,g41)
    c: Equal(g40,g42)
    c: InternalAlignment(g40,g43)
    c: InternalAlignment(g41,g43)
    c: InternalAlignment(g42,g43)
    c: InternalAlignment(g44,g43)
    c: InternalAlignment(g45,g43)
    c: Weight(g46) = 1
    c: Equal(g46,g47)
    c: Equal(g46,g48)
    c: InternalAlignment(g46,g49)
    c: InternalAlignment(g47,g49)
    c: InternalAlignment(g48,g49)
    c: InternalAlignment(g50,g49)
    c: InternalAlignment(g51,g49)
    c: Block(g43)
    c: Block(g49)
    c: Coincident(g52,g7)
    c: Coincident(g52,g6)
    c: Horizontal(g52)
    c: Distance(g52) = 450
    c: Coincident(g53,g7)
    c: Coincident(g53,g6)
    c: Horizontal(g53)
    c: Horizontal(g54)
    c: Coincident(g5,g54)
    c: Block(g54)
    c: Coincident(g1,g54)
    c: Weight(g55) = 1
    c: Equal(g55,g56)
    c: Equal(g55,g57)
    c: InternalAlignment(g55,g58)
    c: InternalAlignment(g56,g58)
    c: InternalAlignment(g57,g58)
    c: InternalAlignment(g59,g58)
    c: InternalAlignment(g60,g58)
    c: Block(g58)
    c: Weight(g61) = 1
    c: Equal(g61,g62)
    c: Equal(g61,g63)
    c: InternalAlignment(g61,g64)
    c: InternalAlignment(g62,g64)
    c: InternalAlignment(g63,g64)
    c: InternalAlignment(g65,g64)
    c: InternalAlignment(g66,g64)
    c: Block(g64)
    c: Weight(g67) = 1
    c: Equal(g67,g68)
    c: Equal(g67,g69)
    c: InternalAlignment(g67,g70)
    c: InternalAlignment(g68,g70)
    c: InternalAlignment(g69,g70)
    c: InternalAlignment(g71,g70)
    c: InternalAlignment(g72,g70)
    c: Block(g70)
    c: Weight(g73) = 1
    c: Equal(g73,g74)
    c: Equal(g73,g75)
    c: InternalAlignment(g73,g76)
    c: InternalAlignment(g74,g76)
    c: InternalAlignment(g75,g76)
    c: InternalAlignment(g77,g76)
    c: InternalAlignment(g78,g76)
    c: Block(g76)
    c: Weight(g79) = 1
    c: Equal(g79,g80)
    c: Equal(g79,g81)
    c: InternalAlignment(g79,g82)
    c: InternalAlignment(g80,g82)
    c: InternalAlignment(g81,g82)
    c: InternalAlignment(g83,g82)
    c: InternalAlignment(g84,g82)
    c: Weight(g85) = 1
    c: Equal(g85,g86)
    c: Equal(g85,g87)
    c: InternalAlignment(g85,g88)
    c: InternalAlignment(g86,g88)
    c: InternalAlignment(g87,g88)
    c: InternalAlignment(g89,g88)
    c: InternalAlignment(g90,g88)
    c: Block(g82)
    c: Block(g88)
    c: Coincident(g91,g82)
    c: Coincident(g91,g88)
    c: Vertical(g91)
    c: Coincident(g92,g82)
    c: Coincident(g92,g64)
    c: Coincident(g93,g64)
    c: Coincident(g93,g88)
    c: Weight(g94) = 1
    c: Equal(g94,g95)
    c: Equal(g94,g96)
    c: InternalAlignment(g94,g97)
    c: InternalAlignment(g95,g97)
    c: InternalAlignment(g96,g97)
    c: InternalAlignment(g98,g97)
    c: InternalAlignment(g99,g97)
    c: Weight(g100) = 1
    c: Equal(g100,g101)
    c: Equal(g100,g102)
    c: InternalAlignment(g100,g103)
    c: InternalAlignment(g101,g103)
    c: InternalAlignment(g102,g103)
    c: InternalAlignment(g104,g103)
    c: InternalAlignment(g105,g103)
    c: Block(g97)
    c: Block(g103)
    c: Coincident(g106,g97)
    c: Coincident(g106,g103)
    c: Vertical(g106)
    c: Coincident(g107,g97)
    c: Coincident(g107,g58)
    c: Coincident(g108,g58)
    c: Coincident(g108,g103)
    c: Weight(g109) = 1
    c: Equal(g109,g110)
    c: Equal(g109,g111)
    c: InternalAlignment(g109,g112)
    c: InternalAlignment(g110,g112)
    c: InternalAlignment(g111,g112)
    c: InternalAlignment(g113,g112)
    c: InternalAlignment(g114,g112)
    c: Weight(g115) = 1
    c: Equal(g115,g116)
    c: Equal(g115,g117)
    c: InternalAlignment(g115,g118)
    c: InternalAlignment(g116,g118)
    c: InternalAlignment(g117,g118)
    c: InternalAlignment(g119,g118)
    c: InternalAlignment(g120,g118)
    c: Block(g112)
    c: Block(g118)
    c: Coincident(g121,g112)
    c: Coincident(g121,g118)
    c: Vertical(g121)
    c: Coincident(g122,g118)
    c: Coincident(g122,g76)
    c: Coincident(g123,g76)
    c: Coincident(g123,g112)
    c: Weight(g124) = 1
    c: Equal(g124,g125)
    c: Equal(g124,g126)
    c: InternalAlignment(g124,g127)
    c: InternalAlignment(g125,g127)
    c: InternalAlignment(g126,g127)
    c: InternalAlignment(g128,g127)
    c: InternalAlignment(g129,g127)
    c: Weight(g130) = 1
    c: Equal(g130,g131)
    c: Equal(g130,g132)
    c: InternalAlignment(g130,g133)
    c: InternalAlignment(g131,g133)
    c: InternalAlignment(g132,g133)
    c: InternalAlignment(g134,g133)
    c: InternalAlignment(g135,g133)
    c: Block(g127)
    c: Block(g133)
    c: Coincident(g136,g127)
    c: Coincident(g136,g133)
    c: Vertical(g136)
    c: Coincident(g137,g133)
    c: Coincident(g137,g70)
    c: Coincident(g138,g70)
    c: Coincident(g138,g127)
    c: Weight(g139) = 1
    c: Equal(g139,g140)
    c: Equal(g139,g141)
    c: InternalAlignment(g139,g142)
    c: InternalAlignment(g140,g142)
    c: InternalAlignment(g141,g142)
    c: InternalAlignment(g143,g142)
    c: InternalAlignment(g144,g142)
    c: Weight(g145) = 1
    c: Equal(g145,g146)
    c: Equal(g145,g147)
    c: InternalAlignment(g145,g148)
    c: InternalAlignment(g146,g148)
    c: InternalAlignment(g147,g148)
    c: InternalAlignment(g149,g148)
    c: InternalAlignment(g150,g148)
    c: Weight(g151) = 1
    c: Equal(g151,g152)
    c: Equal(g151,g153)
    c: InternalAlignment(g151,g154)
    c: InternalAlignment(g152,g154)
    c: InternalAlignment(g153,g154)
    c: InternalAlignment(g155,g154)
    c: InternalAlignment(g156,g154)
    c: Weight(g157) = 1
    c: Equal(g157,g158)
    c: Equal(g157,g159)
    c: InternalAlignment(g157,g160)
    c: InternalAlignment(g158,g160)
    c: InternalAlignment(g159,g160)
    c: InternalAlignment(g161,g160)
    c: InternalAlignment(g162,g160)
    c: Block(g160)
    c: Block(g154)
    c: Block(g148)
    c: Block(g142)
    c: Coincident(g163,g37)
    c: Coincident(g163,g160)
    c: Coincident(g164,g160)
    c: Coincident(g164,g154)
    c: Horizontal(g164)
    c: Coincident(g165,g154)
    c: Coincident(g165,g37)
    c: Vertical(g165)
    c: Coincident(g166,g31)
    c: Coincident(g166,g148)
    c: Vertical(g166)
    c: Coincident(g167,g148)
    c: Coincident(g167,g142)
    c: Horizontal(g167)
    c: Coincident(g168,g142)
    c: Coincident(g168,g31)
    c: Weight(g169) = 1
    c: Equal(g169,g170)
    c: Equal(g169,g171)
    c: InternalAlignment(g169,g172)
    c: InternalAlignment(g170,g172)
    c: InternalAlignment(g171,g172)
    c: InternalAlignment(g173,g172)
    c: InternalAlignment(g174,g172)
    c: Weight(g175) = 1
    c: Equal(g175,g176)
    c: Equal(g175,g177)
    c: InternalAlignment(g175,g178)
    c: InternalAlignment(g176,g178)
    c: InternalAlignment(g177,g178)
    c: InternalAlignment(g179,g178)
    c: InternalAlignment(g180,g178)
    c: Weight(g181) = 1
    c: Equal(g181,g182)
    c: Equal(g181,g183)
    c: InternalAlignment(g181,g184)
    c: InternalAlignment(g182,g184)
    c: InternalAlignment(g183,g184)
    c: InternalAlignment(g185,g184)
    c: InternalAlignment(g186,g184)
    c: Weight(g187) = 1
    c: Equal(g187,g188)
    c: Equal(g187,g189)
    c: InternalAlignment(g187,g190)
    c: InternalAlignment(g188,g190)
    c: InternalAlignment(g189,g190)
    c: InternalAlignment(g191,g190)
    c: InternalAlignment(g192,g190)
    c: Block(g190)
    c: Block(g184)
    c: Block(g178)
    c: Block(g172)
    c: Coincident(g193,g190)
    c: Coincident(g193,g184)
    c: Horizontal(g193)
    c: Coincident(g194,g184)
    c: Coincident(g194,g19)
    c: Vertical(g194)
    c: Coincident(g195,g25)
    c: Coincident(g195,g178)
    c: Vertical(g195)
    c: Coincident(g196,g178)
    c: Coincident(g196,g172)
    c: Horizontal(g196)
    c: Coincident(g197,g172)
    c: Coincident(g197,g25)
    c: Coincident(g198,g19)
    c: Weight(g199) = 1
    c: Equal(g199,g200)
    c: Equal(g199,g201)
    c: InternalAlignment(g199,g202)
    c: InternalAlignment(g200,g202)
    c: InternalAlignment(g201,g202)
    c: InternalAlignment(g203,g202)
    c: InternalAlignment(g204,g202)
    c: Weight(g205) = 1
    c: Equal(g205,g206)
    c: Equal(g205,g207)
    c: InternalAlignment(g205,g208)
    c: InternalAlignment(g206,g208)
    c: InternalAlignment(g207,g208)
    c: InternalAlignment(g209,g208)
    c: InternalAlignment(g210,g208)
    c: Block(g208)
    c: Block(g202)
    c: Coincident(g211,g208)
    c: Coincident(g211,g43)
    c: Coincident(g212,g43)
    c: Coincident(g212,g202)
    c: Coincident(g213,g202)
    c: Coincident(g213,g208)
    c: Vertical(g213)
    c: Weight(g214) = 1
    c: Equal(g214,g215)
    c: Equal(g214,g216)
    c: InternalAlignment(g214,g217)
    c: InternalAlignment(g215,g217)
    c: InternalAlignment(g216,g217)
    c: InternalAlignment(g218,g217)
    c: InternalAlignment(g219,g217)
    c: Weight(g220) = 1
    c: Equal(g220,g221)
    c: Equal(g220,g222)
    c: InternalAlignment(g220,g223)
    c: InternalAlignment(g221,g223)
    c: InternalAlignment(g222,g223)
    c: InternalAlignment(g224,g223)
    c: InternalAlignment(g225,g223)
    c: Block(g223)
    c: Block(g217)
    c: Coincident(g226,g217)
    c: Coincident(g226,g49)
    c: Coincident(g227,g49)
    c: Coincident(g227,g223)
    c: Coincident(g228,g223)
    c: Coincident(g228,g217)
    c: Vertical(g228)
    c: Horizontal(g229)
    c: Block(g229)
    c: Vertical(g230)
    c: Block(g230)
    c: Block(g231)
    c: Weight(g232) = 1
    c: Equal(g232,g233)
    c: Equal(g232,g234)
    c: InternalAlignment(g232,g235)
    c: InternalAlignment(g233,g235)
    c: InternalAlignment(g234,g235)
    c: InternalAlignment(g236,g235)
    c: InternalAlignment(g237,g235)
    c: Weight(g238) = 1
    c: Equal(g238,g239)
    c: Equal(g238,g240)
    c: InternalAlignment(g238,g241)
    c: InternalAlignment(g239,g241)
    c: InternalAlignment(g240,g241)
    c: InternalAlignment(g242,g241)
    c: InternalAlignment(g243,g241)
    c: Weight(g244) = 1
    c: Equal(g244,g245)
    c: Equal(g244,g246)
    c: InternalAlignment(g244,g247)
    c: InternalAlignment(g245,g247)
    c: InternalAlignment(g246,g247)
    c: InternalAlignment(g248,g247)
    c: InternalAlignment(g249,g247)
    c: Weight(g250) = 1
    c: Equal(g250,g251)
    c: Equal(g250,g252)
    c: InternalAlignment(g250,g253)
    c: InternalAlignment(g251,g253)
    c: InternalAlignment(g252,g253)
    c: InternalAlignment(g254,g253)
    c: InternalAlignment(g255,g253)
    c: Block(g235)
    c: Block(g241)
    c: Block(g247)
    c: Block(g253)
    c: Coincident(g256,g241)
    c: Coincident(g256,g235)
    c: Horizontal(g256)
    c: Block(g198)
    c: Weight(g257) = 1
    c: Equal(g257,g258)
    c: Equal(g257,g259)
    c: InternalAlignment(g257,g260)
    c: InternalAlignment(g258,g260)
    c: InternalAlignment(g259,g260)
    c: InternalAlignment(g261,g260)
    c: InternalAlignment(g262,g260)
    c: Weight(g263) = 1
    c: Equal(g263,g264)
    c: Equal(g263,g265)
    c: InternalAlignment(g263,g266)
    c: InternalAlignment(g264,g266)
    c: InternalAlignment(g265,g266)
    c: InternalAlignment(g267,g266)
    c: InternalAlignment(g268,g266)
    c: Weight(g269) = 1
    c: Equal(g269,g270)
    c: Equal(g269,g271)
    c: InternalAlignment(g269,g272)
    c: InternalAlignment(g270,g272)
    c: InternalAlignment(g271,g272)
    c: InternalAlignment(g273,g272)
    c: InternalAlignment(g274,g272)
    c: Weight(g275) = 1
    c: Equal(g275,g276)
    c: Equal(g275,g277)
    c: InternalAlignment(g275,g278)
    c: InternalAlignment(g276,g278)
    c: InternalAlignment(g277,g278)
    c: InternalAlignment(g279,g278)
    c: InternalAlignment(g280,g278)
    c: Block(g260)
    c: Block(g266)
    c: Block(g272)
    c: Block(g278)
    c: Coincident(g281,g272)
    c: Coincident(g281,g278)
    c: Horizontal(g281)
    c: Coincident(g282,g278)
    c: Coincident(g282,g260)
    c: Vertical(g282)
    c: Coincident(g283,g260)
    c: Coincident(g283,g266)
    c: Coincident(g284,g266)
    c: Coincident(g284,g272)
    c: Vertical(g284)
    c: Weight(g285) = 1
    c: Equal(g285,g286)
    c: Equal(g285,g287)
    c: InternalAlignment(g285,g288)
    c: InternalAlignment(g286,g288)
    c: InternalAlignment(g287,g288)
    c: InternalAlignment(g289,g288)
    c: InternalAlignment(g290,g288)
    c: Weight(g291) = 1
    c: Equal(g291,g292)
    c: Equal(g291,g293)
    c: InternalAlignment(g291,g294)
    c: InternalAlignment(g292,g294)
    c: InternalAlignment(g293,g294)
    c: InternalAlignment(g295,g294)
    c: InternalAlignment(g296,g294)
    c: Weight(g297) = 1
    c: Equal(g297,g298)
    c: Equal(g297,g299)
    c: InternalAlignment(g297,g300)
    c: InternalAlignment(g298,g300)
    c: InternalAlignment(g299,g300)
    c: InternalAlignment(g301,g300)
    c: InternalAlignment(g302,g300)
    c: Block(g300)
    c: Block(g294)
    c: Block(g288)
    c: Coincident(g303,g294)
    c: Coincident(g303,g288)
    c: Coincident(g304,g288)
    c: Coincident(g304,g300)
    c: Vertical(g304)
    c: Coincident(g305,g300)
    c: Coincident(g305,g294)
    c: Horizontal(g305)
    c: Weight(g306) = 1
    c: Equal(g306,g307)
    c: InternalAlignment(g306,g308)
    c: InternalAlignment(g307,g308)
    c: InternalAlignment(g309,g308)
    c: InternalAlignment(g310,g308)
    c: Weight(g311) = 1
    c: Equal(g311,g312)
    c: Equal(g311,g313)
    c: InternalAlignment(g311,g314)
    c: InternalAlignment(g312,g314)
    c: InternalAlignment(g313,g314)
    c: InternalAlignment(g315,g314)
    c: InternalAlignment(g316,g314)
    c: Weight(g317) = 1
    c: Equal(g317,g318)
    c: Equal(g317,g319)
    c: InternalAlignment(g317,g320)
    c: InternalAlignment(g318,g320)
    c: InternalAlignment(g319,g320)
    c: InternalAlignment(g321,g320)
    c: InternalAlignment(g322,g320)
    c: Equal(g323,g324)
    c: Equal(g323,g325)
    c: InternalAlignment(g323,g326)
    c: InternalAlignment(g324,g326)
    c: InternalAlignment(g325,g326)
    c: InternalAlignment(g327,g326)
    c: InternalAlignment(g328,g326)
    c: Block(g314)
    c: Block(g320)
    c: Block(g326)
    c: Block(g308)
    c: Coincident(g329,g308)
    c: Coincident(g329,g314)
    c: Horizontal(g329)
    c: Coincident(g330,g314)
    c: Coincident(g330,g320)
    c: Vertical(g330)
    c: Coincident(g331,g320)
    c: Coincident(g331,g326)
    c: Horizontal(g331)
    c: Coincident(g332,g326)
    c: Coincident(g332,g308)
    c: Vertical(g333)
    c: Vertical(g334)
    c: Horizontal(g335)
    c: Horizontal(g336)
    c: Distance(g336) = 4
    c: Distance(g335) = 4
    c: Distance(g337) = 4
    c: Distance(g338) = 4
    c: Distance(g333) = 4
    c: Distance(g334) = 4
    c: Parallel(g3,g338)
    c: Parallel(g337,g3)
FEATURE [Sketcher::SketchObject] Sketch001
  FullyConstrained = true
  MapMode = 4
  Placement = pos=(0,0,0) rot=(0.57735,0.57735,0.57735;2.0944rad)
  Support = -> [Sketch]
  sketch-geometry (46):
    g0: BSplineCurve PolesCount=3 KnotsCount=2 Degree=2 IsPeriodic=0
    g1: ArcOfCircle CenterX=73.1223 CenterY=-32.291 CenterZ=0 NormalX=0 NormalY=0 NormalZ=1 AngleXU=0 Radius=13 StartAngle=5.92268 EndAngle=9.06428
    g2: ArcOfCircle CenterX=66.7816 CenterY=-49.1439 CenterZ=0 NormalX=0 NormalY=0 NormalZ=1 AngleXU=0 Radius=13 StartAngle=2.78068 EndAngle=5.92131
    g3: ArcOfCircle CenterX=55.9263 CenterY=-78.1807 CenterZ=0 NormalX=0 NormalY=0 NormalZ=1 AngleXU=0 Radius=13 StartAngle=5.92268 EndAngle=9.06428
    g4: ArcOfCircle CenterX=49.5884 CenterY=-95.0342 CenterZ=0 NormalX=0 NormalY=0 NormalZ=1 AngleXU=0 Radius=13 StartAngle=2.78068 EndAngle=5.92131
    g5: ArcOfCircle CenterX=38.7206 CenterY=-124.067 CenterZ=0 NormalX=0 NormalY=0 NormalZ=1 AngleXU=0 Radius=13 StartAngle=5.92268 EndAngle=9.06428
    g6: ArcOfCircle CenterX=32.3875 CenterY=-140.92 CenterZ=0 NormalX=0 NormalY=0 NormalZ=1 AngleXU=0 Radius=13 StartAngle=2.78068 EndAngle=5.92131
    g7: ArcOfCircle CenterX=21.4715 CenterY=-169.934 CenterZ=0 NormalX=0 NormalY=0 NormalZ=1 AngleXU=0 Radius=13 StartAngle=5.92268 EndAngle=9.06428
    g8: ArcOfCircle CenterX=15.1336 CenterY=-186.787 CenterZ=0 NormalX=0 NormalY=0 NormalZ=1 AngleXU=0 Radius=13 StartAngle=2.78068 EndAngle=5.92131
    g9-g12: Circle x4 (B-spline internal-alignment scaffolding for g13; pole/knot coordinates omitted)
    g13: BSplineCurve PolesCount=4 KnotsCount=2 Degree=3 IsPeriodic=0
    g14: GeomPoint X=28.8094 Y=-19.0875 Z=0
    g15: GeomPoint X=47.0443 Y=-50.4712 Z=0
    g16: Circle CenterX=53.5586 CenterY=-23.2695 CenterZ=0 NormalX=0 NormalY=0 NormalZ=1 AngleXU=0 Radius=3.24518
    g17: Circle CenterX=-195.441 CenterY=-127.082 CenterZ=0 NormalX=0 NormalY=0 NormalZ=1 AngleXU=0 Radius=1
    g18: Circle CenterX=-8.24091 CenterY=-197.481 CenterZ=0 NormalX=0 NormalY=0 NormalZ=1 AngleXU=0 Radius=1
    g19: Circle CenterX=12.8789 CenterY=-141.321 CenterZ=0 NormalX=0 NormalY=0 NormalZ=1 AngleXU=0 Radius=1
    g20: BSplineCurve PolesCount=3 KnotsCount=2 Degree=2 IsPeriodic=0
    g21: GeomPoint X=-195.441 Y=-127.082 Z=0
    g22: GeomPoint X=12.8789 Y=-141.321 Z=0
    g23: Circle CenterX=-12.8016 CenterY=-179.036 CenterZ=0 NormalX=0 NormalY=0 NormalZ=1 AngleXU=0 Radius=10.5072
    g24: Circle CenterX=0.933922 CenterY=-166.43 CenterZ=0 NormalX=0 NormalY=0 NormalZ=1 AngleXU=0 Radius=3.26661
    g25: Circle CenterX=-33.5518 CenterY=-176.44 CenterZ=0 NormalX=0 NormalY=0 NormalZ=1 AngleXU=0 Radius=5.64388
    g26: Circle CenterX=-47.2366 CenterY=-173.859 CenterZ=0 NormalX=0 NormalY=0 NormalZ=1 AngleXU=0 Radius=3.01653
    g27: Circle CenterX=-56.2595 CenterY=-171.456 CenterZ=0 NormalX=0 NormalY=0 NormalZ=1 AngleXU=0 Radius=2.12826
    g28: ArcOfCircle CenterX=51.2151 CenterY=-198.473 CenterZ=0 NormalX=0 NormalY=0 NormalZ=1 AngleXU=0 Radius=20 StartAngle=2.78189 EndAngle=4.35269
    g29: LineSegment StartX=32.4951 StartY=-191.433 StartZ=0 EndX=94.6578 EndY=-26.1352 EndZ=0
    g30: LineSegment StartX=43.1192 StartY=-220.001 StartZ=0 EndX=-196.497 EndY=-129.89 EndZ=0
    g31: LineSegment StartX=43.1192 StartY=-220.001 StartZ=0 EndX=44.1752 EndY=-217.193 EndZ=0
    g32: LineSegment StartX=117.223 StartY=-19.0875 StartZ=0 EndX=117.223 EndY=-16.0875 EndZ=0
    g33: LineSegment StartX=117.223 StartY=-16.0875 StartZ=0 EndX=17.2232 EndY=-16.0875 EndZ=0
    g34: LineSegment StartX=17.2232 StartY=-16.0875 StartZ=0 EndX=17.2232 EndY=-19.0875 EndZ=0
    g35: LineSegment StartX=28.8094 StartY=-19.0875 StartZ=0 EndX=17.2232 EndY=-19.0875 EndZ=0
    g36: LineSegment StartX=47.0443 StartY=-50.4712 StartZ=0 EndX=12.8789 EndY=-141.321 EndZ=0
    g37: LineSegment StartX=-195.441 StartY=-127.082 StartZ=0 EndX=-196.497 EndY=-129.89 EndZ=0
    g38: LineSegment StartX=85.2866 StartY=-36.8766 StartZ=0 EndX=78.9396 EndY=-53.7463 EndZ=0
    g39: LineSegment StartX=60.9579 StartY=-27.7053 StartZ=0 EndX=54.6191 EndY=-44.5532 EndZ=0
    g40: LineSegment StartX=68.0907 StartY=-82.7664 StartZ=0 EndX=61.7465 EndY=-99.6365 EndZ=0
    g41: LineSegment StartX=43.7619 StartY=-73.595 StartZ=0 EndX=37.426 EndY=-90.4435 EndZ=0
    g42: LineSegment StartX=50.885 StartY=-128.652 StartZ=0 EndX=44.5456 EndY=-145.522 EndZ=0
    g43: LineSegment StartX=26.5562 StartY=-119.481 StartZ=0 EndX=20.2251 EndY=-136.329 EndZ=0
    g44: LineSegment StartX=9.3071 StartY=-165.349 StartZ=0 EndX=2.97115 EndY=-182.197 EndZ=0
    g45: LineSegment StartX=33.6358 StartY=-174.52 StartZ=0 EndX=27.2917 EndY=-191.39 EndZ=0
  constraints (71):
    c: Block(g0)
    c: Block(g1)
    c: Block(g2)
    c: Block(g4)
    c: Block(g3)
    c: Block(g6)
    c: Block(g5)
    c: Block(g8)
    c: Block(g7)
    c: Weight(g9) = 1
    c: Equal(g9,g10)
    c: Equal(g9,g11)
    c: Equal(g9,g12)
    c: InternalAlignment(g9-g12 -> g13) x4
    c: InternalAlignment(g14,g13)
    c: InternalAlignment(g15,g13)
    c: Block(g16)
    c: Weight(g17) = 1
    c: Equal(g17,g18)
    c: Equal(g17,g19)
    c: InternalAlignment(g17,g20)
    c: InternalAlignment(g18,g20)
    c: InternalAlignment(g19,g20)
    c: InternalAlignment(g21,g20)
    c: InternalAlignment(g22,g20)
    c: Block(g20)
    c: Block(g23)
    c: Block(g24)
    c: Block(g25)
    c: Block(g26)
    c: Block(g27)
    c: Block(g28)
    c: Coincident(g29,g28)
    c: Coincident(g29,g0)
    c: Block(g13)
    c: Coincident(g31,g30)
    c: Coincident(g31,g28)
    c: Block(g31)
    c: Coincident(g32,g0)
    c: Vertical(g32)
    c: Coincident(g33,g32)
    c: Horizontal(g33)
    c: Coincident(g34,g33)
    c: Vertical(g34)
    c: Block(g33)
    c: Coincident(g35,g13)
    c: Coincident(g35,g34)
    c: Horizontal(g35)
    c: Coincident(g36,g13)
    c: Coincident(g36,g20)
    c: Coincident(g37,g20)
    c: Coincident(g37,g30)
    c: Block(g30)
    c: Coincident(g38,g1)
    c: Coincident(g38,g2)
    c: Coincident(g39,g1)
    c: Coincident(g39,g2)
    c: Coincident(g40,g3)
    c: Coincident(g40,g4)
    c: Coincident(g41,g3)
    c: Coincident(g41,g4)
    c: Coincident(g42,g5)
    c: Coincident(g42,g6)
    c: Coincident(g43,g5)
    c: Coincident(g43,g6)
    c: Coincident(g44,g7)
    c: Coincident(g44,g8)
    c: Coincident(g45,g7)
    c: Coincident(g45,g8)
    c: Distance(g30) = 256
    c: Distance(g33) = 100
FEATURE [Part::Extrusion] Extrude002
  Base = -> Sketch001
  Dir = (1,0,0)
  DirMode = 2
  FaceMakerClass = Part::FaceMakerBullseye
  LengthFwd = 8
  LengthRev = 0
  Solid = true
  Symmetric = false
FEATURE [Sketcher::SketchObject] Sketch002
  FullyConstrained = true
  sketch-geometry (20):
    g0: LineSegment StartX=-2.77179 StartY=-200.304 StartZ=0 EndX=5.22821 EndY=-200.304 EndZ=0
    g1: LineSegment StartX=5.22821 StartY=-200.304 StartZ=0 EndX=5.22821 EndY=-197.304 EndZ=0
    g2: LineSegment StartX=-2.77179 StartY=-200.304 StartZ=0 EndX=-2.77179 EndY=-197.304 EndZ=0
    g3: LineSegment StartX=5.22821 StartY=-197.304 StartZ=0 EndX=8.22821 EndY=-197.304 EndZ=0
    g4: LineSegment StartX=-2.77179 StartY=-197.304 StartZ=0 EndX=-5.77179 EndY=-197.304 EndZ=0
    g5: LineSegment StartX=19.2282 StartY=-203.304 StartZ=0 EndX=19.2282 EndY=-206.304 EndZ=0
    g6: LineSegment StartX=-16.7718 StartY=-203.304 StartZ=0 EndX=-16.7718 EndY=-206.304 EndZ=0
    g7: LineSegment StartX=-16.7718 StartY=-206.304 StartZ=0 EndX=19.2282 EndY=-206.304 EndZ=0
    g8: Circle CenterX=-16.7718 CenterY=-203.304 CenterZ=0 NormalX=0 NormalY=0 NormalZ=1 AngleXU=0 Radius=1
    g9: Circle CenterX=-5.77179 CenterY=-203.304 CenterZ=0 NormalX=0 NormalY=0 NormalZ=1 AngleXU=0 Radius=1
    g10: Circle CenterX=-5.77179 CenterY=-197.304 CenterZ=0 NormalX=0 NormalY=0 NormalZ=1 AngleXU=0 Radius=1
    g11: BSplineCurve PolesCount=3 KnotsCount=2 Degree=2 IsPeriodic=0
    g12: GeomPoint X=-16.7718 Y=-203.304 Z=0
    g13: GeomPoint X=-5.77179 Y=-197.304 Z=0
    g14: Circle CenterX=19.2282 CenterY=-203.304 CenterZ=0 NormalX=0 NormalY=0 NormalZ=1 AngleXU=0 Radius=1
    g15: Circle CenterX=8.22821 CenterY=-203.304 CenterZ=0 NormalX=0 NormalY=0 NormalZ=1 AngleXU=0 Radius=1
    g16: Circle CenterX=8.22821 CenterY=-197.304 CenterZ=0 NormalX=0 NormalY=0 NormalZ=1 AngleXU=0 Radius=1
    g17: BSplineCurve PolesCount=3 KnotsCount=2 Degree=2 IsPeriodic=0
    g18: GeomPoint X=19.2282 Y=-203.304 Z=0
    g19: GeomPoint X=8.22821 Y=-197.304 Z=0
  constraints (41):
    c: Horizontal(g0)
    c: Distance(g0) = 8
    c: Coincident(g1,g0)
    c: Vertical(g1)
    c: Distance(g1) = 3
    c: Coincident(g2,g0)
    c: Vertical(g2)
    c: Distance(g2) = 3
    c: Coincident(g3,g1)
    c: Horizontal(g3)
    c: Distance(g3) = 3
    c: Coincident(g4,g2)
    c: Horizontal(g4)
    c: Distance(g4) = 3
    c: Vertical(g5)
    c: Vertical(g6)
    c: Coincident(g7,g6)
    c: Coincident(g7,g5)
    c: Weight(g8) = 1
    c: Equal(g8,g9)
    c: Equal(g8,g10)
    c: Coincident(g11,g4)
    c: InternalAlignment(g8,g11)
    c: InternalAlignment(g9,g11)
    c: InternalAlignment(g10,g11)
    c: InternalAlignment(g12,g11)
    c: InternalAlignment(g13,g11)
    c: Coincident(g17,g5)
    c: Weight(g14) = 1
    c: Equal(g14,g15)
    c: Equal(g14,g16)
    c: Coincident(g17,g3)
    c: InternalAlignment(g14,g17)
    c: InternalAlignment(g15,g17)
    c: InternalAlignment(g16,g17)
    c: InternalAlignment(g18,g17)
    c: InternalAlignment(g19,g17)
    c: Block(g7)
    c: Block(g17)
    c: Block(g11)
    c: Block(g6)
FEATURE [Part::Extrusion] Extrude003
  Base = -> Sketch002
  Dir = (0,0,1)
  DirMode = 2
  FaceMakerClass = Part::FaceMakerBullseye
  LengthFwd = 260
  LengthRev = 0
  Solid = true
  Symmetric = false
FEATURE [Part::Extrusion] Extrude
  Base = -> Sketch
  Dir = (0,0,1)
  DirMode = 2
  FaceMakerClass = Part::FaceMakerBullseye
  LengthFwd = 14
  LengthRev = 0
  Solid = true
  Symmetric = false
